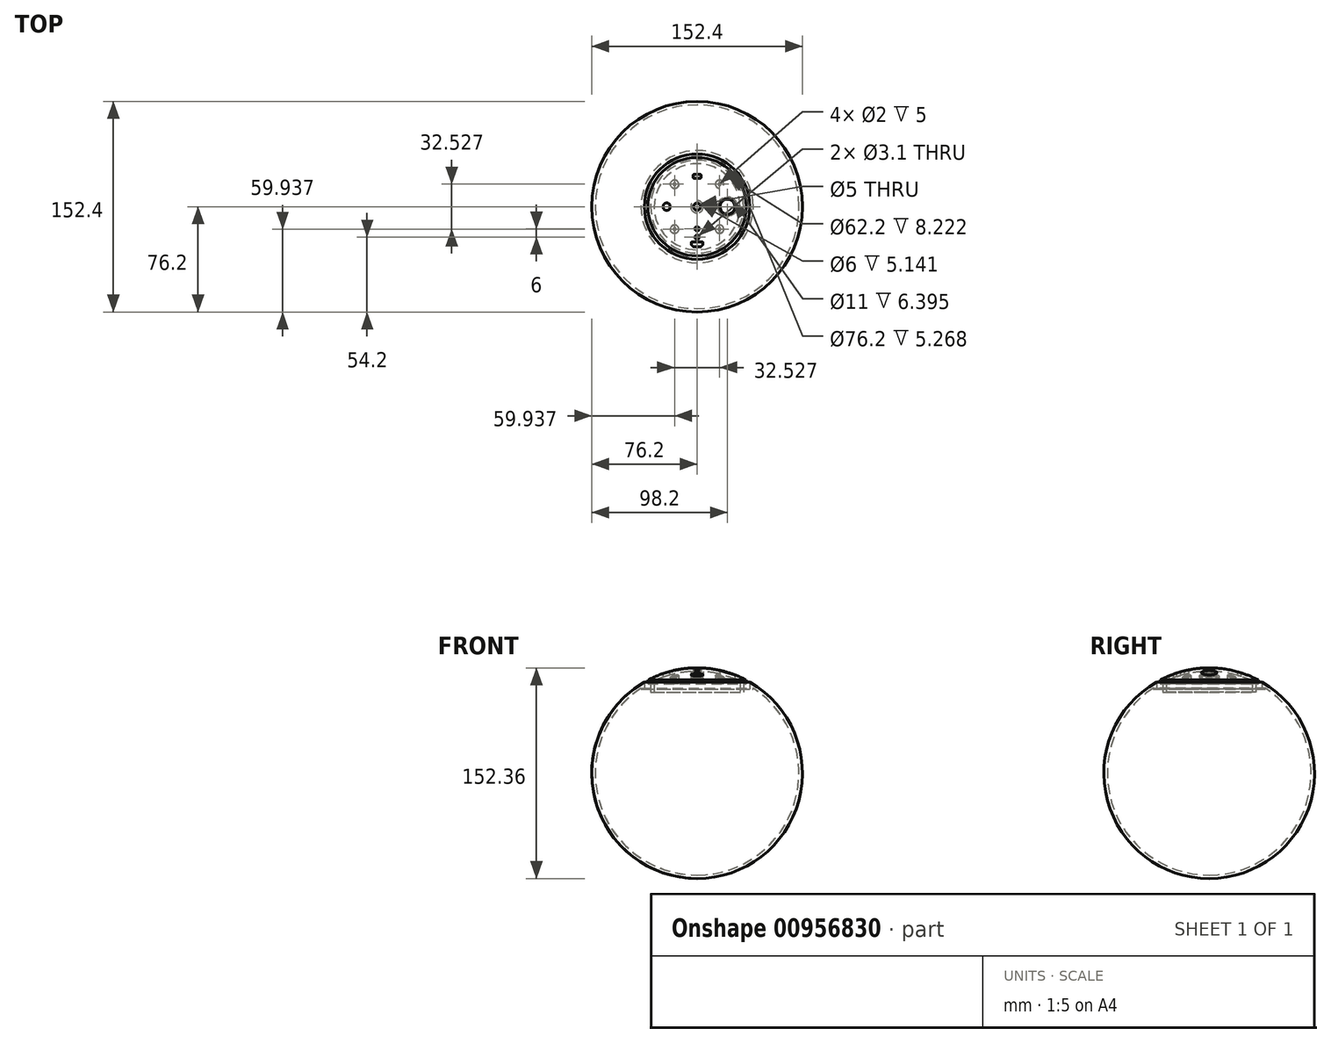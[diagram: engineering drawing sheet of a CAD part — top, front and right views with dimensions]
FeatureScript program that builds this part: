
annotation { "Feature Type Name" : "Feature", "Feature Type Description" : "" }
export const myFeature = defineFeature(function(context is Context, id is Id, definition is map)
    precondition{}
    {
        {
            var Q0;
            Q0=qCreatedBy(makeId("Front.planeOp"),FACE);
            var sketch = newSketch(context, id + "F0", { "sketchPlane" : qUnion([Q0])});
            skArc(sketch, "E0", {"start": v(-38.1, 66) * mm, "mid": v(-73.6, -19.72) * mm, "end": v(0, -76.2) * mm});
            skLineSegment(sketch, "E1", {"start": v(0, 0) * mm, "end": v(0, 126.02) * mm, "construction": true});
            skLineSegment(sketch, "E2.0", {"start": v(38.1, 0) * mm, "end": v(38.1, 126.02) * mm, "construction": true});
            skLineSegment(sketch, "E3.0", {"start": v(-38.1, 0) * mm, "end": v(-38.1, 126.02) * mm, "construction": true});
            skLineSegment(sketch, "E4", {"start": v(0, 0) * mm, "end": v(0, -76.2) * mm, "construction": true});
            skLineSegment(sketch, "E5", {"start": v(0, -76.2) * mm, "end": v(0, -73.7) * mm});
            skLineSegment(sketch, "E6.0", {"start": v(-40.6, 0) * mm, "end": v(-40.6, 61.5) * mm});
            skLineSegment(sketch, "E7", {"start": v(-40.6, 60.72) * mm, "end": v(-38.1, 60.72) * mm});
            skLineSegment(sketch, "E8", {"start": v(-38.1, 60.72) * mm, "end": v(-38.1, 66) * mm});
            skArc(sketch, "E9.trimOffspring", {"start": v(-40.6, 61.5) * mm, "mid": v(-70.59, -21.2) * mm, "end": v(0, -73.7) * mm});
            skSolve(sketch);
        }
        {
            var Q0;
            {var subQ5=sQuery(id+"F0.wireOp",EDGE,"E0");Q0=makeQuery(id+"F0.imprint","IMPRINT",FACE,{"disambiguationData":[TD([[makeQuery(id+"F0.imprint","IMPRINT",EDGE,{"derivedFrom":subQ5}),1.0]])]});}
            var Q1;
            Q1=sQuery(id+"F0.wireOp",EDGE,"E1");
            revolve(context, id + "F1", {"surfaceOperationType" : NewSurfaceOperationType.NEW, "entities" : qUnion([Q0]), "axis" : qUnion([Q1]), "revolveType" : RevolveType.FULL});
        }
        {
            var Q0;
            Q0=qCreatedBy(makeId("Front.planeOp"),FACE);
            var sketch = newSketch(context, id + "F2", { "sketchPlane" : qUnion([Q0])});
            skArc(sketch, "E10", {"start": v(0, 76.2) * mm, "mid": v(-18.34, 73.96) * mm, "end": v(-35.6, 67.37) * mm});
            skLineSegment(sketch, "E11", {"start": v(0, 0) * mm, "end": v(0, 119.66) * mm, "construction": true});
            skLineSegment(sketch, "E12.0", {"start": v(-38.1, 0) * mm, "end": v(-38.1, 119.66) * mm, "construction": true});
            skArc(sketch, "E13.0", {"start": v(0, 73.7) * mm, "mid": v(-15.93, 71.96) * mm, "end": v(-31.1, 66.82) * mm});
            skLineSegment(sketch, "E14.0", {"start": v(-35.6, 64.53) * mm, "end": v(-35.6, 67.37) * mm});
            skLineSegment(sketch, "E15.0", {"start": v(-33.6, 58.6) * mm, "end": v(-33.6, 65.6) * mm});
            skLineSegment(sketch, "E16.0", {"start": v(-31.1, 58.6) * mm, "end": v(-31.1, 66.82) * mm});
            skArc(sketch, "E17.trimOffspring", {"start": v(-33.6, 65.6) * mm, "mid": v(-34.6, 65.07) * mm, "end": v(-35.6, 64.53) * mm});
            skLineSegment(sketch, "E18", {"start": v(-33.6, 58.6) * mm, "end": v(-31.1, 58.6) * mm});
            skLineSegment(sketch, "E19", {"start": v(0, 76.2) * mm, "end": v(0, 73.7) * mm});
            skSolve(sketch);
        }
        {
            var Q0;
            Q0=qSketchRegion(id+"F2",true);
            var Q1;
            Q1=sQuery(id+"F2.wireOp",EDGE,"E11");
            revolve(context, id + "F3", {"surfaceOperationType" : NewSurfaceOperationType.NEW, "entities" : qUnion([Q0]), "axis" : qUnion([Q1]), "revolveType" : RevolveType.FULL});
        }
        {
            var Q0;
            Q0=qCreatedBy(makeId("Top.planeOp"),FACE);
            cPlane(context, id + "F4", {"entities" : qUnion([Q0]), "cplaneType" : CPlaneType.OFFSET, "offset" : 81.28 * mm, "width" : 152.4 * mm, "height" : 152.4 * mm});
        }
        {
            var Q0;
            Q0=qCreatedBy(id+"F4.planeOp",FACE);
            var sketch = newSketch(context, id + "F5", { "sketchPlane" : qUnion([Q0])});
            skLineSegment(sketch, "E20.bottom", {"start": v(3.7, -25.5) * mm, "end": v(-3.7, -25.5) * mm});
            skLineSegment(sketch, "E20.top", {"start": v(4.2, -27.6) * mm, "end": v(-4.2, -27.6) * mm});
            skLineSegment(sketch, "E20.left", {"start": v(4.2, -26) * mm, "end": v(4.2, -27.42) * mm});
            skLineSegment(sketch, "E20.right", {"start": v(-4.2, -26) * mm, "end": v(-4.2, -27.42) * mm});
            skPoint(sketch, "E20.middle", {"position": v(0, -26.55) * mm});
            skLineSegment(sketch, "E21.0", {"start": v(1.38, -28.9) * mm, "end": v(-1.07, -28.9) * mm, "construction": true});
            skLineSegment(sketch, "E22.0", {"start": v(2.7, -21.08) * mm, "end": v(2.7, -25.34) * mm, "construction": true});
            skLineSegment(sketch, "E23.0", {"start": v(-2.7, -21.08) * mm, "end": v(-2.7, -25.34) * mm, "construction": true});
            skLineSegment(sketch, "E24", {"start": v(-4.06, -27.72) * mm, "end": v(-2.81, -28.8) * mm});
            skLineSegment(sketch, "E25", {"start": v(2.81, -28.8) * mm, "end": v(4.06, -27.72) * mm});
            skLineSegment(sketch, "E26", {"start": v(-2.55, -28.9) * mm, "end": v(2.55, -28.9) * mm});
            skPoint(sketch, "E27.visualSharp", {"position": v(-4.2, -25.5) * mm});
            skArc(sketch, "E27.filletArc", {"start": v(-3.7, -25.5) * mm, "mid": v(-4.05, -25.65) * mm, "end": v(-4.2, -26) * mm});
            skPoint(sketch, "E28.visualSharp", {"position": v(4.2, -25.5) * mm});
            skArc(sketch, "E28.filletArc", {"start": v(4.2, -26) * mm, "mid": v(4.05, -25.65) * mm, "end": v(3.7, -25.5) * mm});
            skPoint(sketch, "E29.visualSharp", {"position": v(4.2, -27.6) * mm});
            skArc(sketch, "E29.filletArc", {"start": v(4.06, -27.72) * mm, "mid": v(4.16, -27.58) * mm, "end": v(4.2, -27.42) * mm});
            skPoint(sketch, "E30.visualSharp", {"position": v(2.7, -28.9) * mm});
            skArc(sketch, "E30.filletArc", {"start": v(2.55, -28.9) * mm, "mid": v(2.7, -28.87) * mm, "end": v(2.81, -28.8) * mm});
            skPoint(sketch, "E31.visualSharp", {"position": v(-2.7, -28.9) * mm});
            skArc(sketch, "E31.filletArc", {"start": v(-2.81, -28.8) * mm, "mid": v(-2.7, -28.87) * mm, "end": v(-2.55, -28.9) * mm});
            skPoint(sketch, "E32.visualSharp", {"position": v(-4.2, -27.6) * mm});
            skArc(sketch, "E32.filletArc", {"start": v(-4.2, -27.42) * mm, "mid": v(-4.16, -27.58) * mm, "end": v(-4.06, -27.72) * mm});
            skSolve(sketch);
        }
        {
            var Q0;
            Q0=qCreatedBy(id+"F4.planeOp",FACE);
            var sketch = newSketch(context, id + "F6", { "sketchPlane" : qUnion([Q0])});
            skCircle(sketch, "E33", {"center": v(0, 0) * mm, "radius": 22 * mm, "construction": true});
            skCircle(sketch, "E34", {"center": v(0, -22) * mm, "radius": 1.55 * mm});
            skLineSegment(sketch, "E35", {"start": v(0, 0) * mm, "end": v(0, -21.23) * mm, "construction": true});
            skCircle(sketch, "E36.0.1.0", {"center": v(0, -16) * mm, "radius": 1.55 * mm});
            skLineSegment(sketch, "E36.direction1", {"start": v(0, -22) * mm, "end": v(25, -22) * mm, "construction": true});
            skLineSegment(sketch, "E36.direction2", {"start": v(0, -22) * mm, "end": v(0, -16) * mm, "construction": true});
            skSolve(sketch);
        }
        {
            var Q0;
            Q0=qCreatedBy(id+"F4.planeOp",FACE);
            var sketch = newSketch(context, id + "F7", { "sketchPlane" : qUnion([Q0])});
            skCircle(sketch, "E37", {"center": v(0, 0) * mm, "radius": 22 * mm, "construction": true});
            skCircle(sketch, "E38", {"center": v(22, 0) * mm, "radius": 5.5 * mm});
            skLineSegment(sketch, "E39.bottom", {"start": v(2.8, 23.4) * mm, "end": v(-2.8, 23.4) * mm});
            skLineSegment(sketch, "E39.top", {"start": v(2.8, 20.6) * mm, "end": v(-2.8, 20.6) * mm});
            skLineSegment(sketch, "E39.left", {"start": v(2.8, 23.4) * mm, "end": v(2.8, 20.6) * mm});
            skLineSegment(sketch, "E39.right", {"start": v(-2.8, 23.4) * mm, "end": v(-2.8, 20.6) * mm});
            skPoint(sketch, "E39.middle", {"position": v(0, 22) * mm});
            skSolve(sketch);
        }
        {
            var Q0;
            Q0=qCreatedBy(id+"F4.planeOp",FACE);
            var sketch = newSketch(context, id + "F8", { "sketchPlane" : qUnion([Q0])});
            skCircle(sketch, "E40", {"center": v(0, 0) * mm, "radius": 22 * mm, "construction": true});
            skArc(sketch, "E41", {"start": v(-24.4, -1.24) * mm, "mid": v(-22, -2.7) * mm, "end": v(-19.6, -1.24) * mm});
            skLineSegment(sketch, "E42", {"start": v(-22, 0) * mm, "end": v(-22, 4.73) * mm, "construction": true});
            skLineSegment(sketch, "E43.0", {"start": v(-24.4, -2.74) * mm, "end": v(-24.4, 4.73) * mm});
            skLineSegment(sketch, "E44.MirrorCS", {"start": v(-19.6, -2.74) * mm, "end": v(-19.6, 4.73) * mm});
            skArc(sketch, "E45.trimOffspring", {"start": v(-19.6, 1.24) * mm, "mid": v(-22, 2.7) * mm, "end": v(-24.4, 1.24) * mm});
            skSolve(sketch);
        }
        {
            var Q0;
            Q0=qCreatedBy(id+"F4.planeOp",FACE);
            var sketch = newSketch(context, id + "F9", { "sketchPlane" : qUnion([Q0])});
            skCircle(sketch, "E46", {"center": v(0, 0) * mm, "radius": 2.5 * mm});
            skSolve(sketch);
        }
        {
            var Q0;
            Q0=qSketchRegion(id+"F9",true);
            extrude(context, id + "F10", {"entities" : qUnion([Q0]), "operationType" : NewBodyOperationType.REMOVE, "oppositeDirection" : true, "depth" : 25 * mm, "offsetDistance" : 25 * mm});
        }
        {
            var Q0;
            Q0=qCreatedBy(makeId("Top.planeOp"),FACE);
            cPlane(context, id + "F11", {"entities" : qUnion([Q0]), "cplaneType" : CPlaneType.OFFSET, "offset" : 70 * mm, "width" : 150 * mm, "height" : 150 * mm});
        }
        {
            var Q0;
            Q0=qCreatedBy(id+"F11.planeOp",FACE);
            var sketch = newSketch(context, id + "F12", { "sketchPlane" : qUnion([Q0])});
            skCircle(sketch, "E47", {"center": v(0, 0) * mm, "radius": 3 * mm});
            skSolve(sketch);
        }
        {
            var Q0;
            Q0=qSketchRegion(id+"F12",true);
            var Q1;
            Q1=makeQuery(id+"F3.opRevolve","SWEPT_FACE",FACE,{"disambiguationData":[OSD([sQuery(id+"F2.wireOp",EDGE,"E10")])]});
            extrude(context, id + "F13", {"entities" : qUnion([Q0]), "operationType" : NewBodyOperationType.REMOVE, "endBound" : BoundingType.UP_TO_SURFACE, "depth" : 25 * mm, "endBoundEntityFace" : qUnion([Q1]), "hasOffset" : true, "offsetDistance" : 1 * mm});
        }
        {
            var Q0;
            Q0=qSketchRegion(id+"F5",true);
            extrude(context, id + "F14", {"entities" : qUnion([Q0]), "operationType" : NewBodyOperationType.REMOVE, "oppositeDirection" : true, "depth" : 25.4 * mm, "offsetDistance" : 25.4 * mm});
        }
        {
            var Q0;
            Q0=qSketchRegion(id+"F6",true);
            var Q1;
            Q1=qSketchRegion(id+"F8",true);
            extrude(context, id + "F15", {"entities" : qUnion([Q0, Q1]), "operationType" : NewBodyOperationType.REMOVE, "oppositeDirection" : true, "depth" : 25 * mm, "offsetDistance" : 25 * mm});
        }
        {
            var Q0;
            Q0=qSketchRegion(id+"F7",true);
            extrude(context, id + "F16", {"entities" : qUnion([Q0]), "operationType" : NewBodyOperationType.REMOVE, "oppositeDirection" : true, "depth" : 25 * mm, "offsetDistance" : 25 * mm});
        }
        {
            var Q0;
            Q0=qCreatedBy(makeId("Top.planeOp"),FACE);
            cPlane(context, id + "F17", {"entities" : qUnion([Q0]), "cplaneType" : CPlaneType.OFFSET, "offset" : 65 * mm, "width" : 150 * mm, "height" : 150 * mm});
        }
        {
            var Q0;
            Q0=qCreatedBy(id+"F17.planeOp",FACE);
            var sketch = newSketch(context, id + "F18", { "sketchPlane" : qUnion([Q0])});
            skCircle(sketch, "E48", {"center": v(-16.26, 16.26) * mm, "radius": 3 * mm});
            skLineSegment(sketch, "E49", {"start": v(0, 0) * mm, "end": v(-28.69, 28.69) * mm, "construction": true});
            skLineSegment(sketch, "E50", {"start": v(0, 0) * mm, "end": v(16.68, 16.68) * mm, "construction": true});
            skCircle(sketch, "E51.1.0", {"center": v(-16.26, -16.26) * mm, "radius": 3 * mm});
            skCircle(sketch, "E51.2.0", {"center": v(16.26, -16.26) * mm, "radius": 3 * mm});
            skCircle(sketch, "E51.3.0", {"center": v(16.26, 16.26) * mm, "radius": 3 * mm});
            skPoint(sketch, "E51.center", {"position": v(0, 0) * mm});
            skSolve(sketch);
        }
        {
            var Q0;
            Q0=qSketchRegion(id+"F18",true);
            var Q1;
            Q1=makeQuery(id+"F3.opRevolve","SWEPT_FACE",FACE,{"disambiguationData":[OSD([sQuery(id+"F2.wireOp",EDGE,"E13.0")])]});
            extrude(context, id + "F19", {"entities" : qUnion([Q0]), "operationType" : NewBodyOperationType.ADD, "endBound" : BoundingType.UP_TO_SURFACE, "depth" : 25 * mm, "endBoundEntityFace" : qUnion([Q1]), "offsetDistance" : 25 * mm});
        }
        {
            var Q0;
            Q0=qCreatedBy(id+"F17.planeOp",FACE);
            var sketch = newSketch(context, id + "F20", { "sketchPlane" : qUnion([Q0])});
            skCircle(sketch, "E52.0", {"center": v(-16.26, 16.26) * mm, "radius": 3 * mm, "construction": true});
            skCircle(sketch, "E53", {"center": v(-16.26, 16.26) * mm, "radius": 1 * mm});
            skCircle(sketch, "E54.1.0", {"center": v(-16.26, -16.26) * mm, "radius": 1 * mm});
            skCircle(sketch, "E54.2.0", {"center": v(16.26, -16.26) * mm, "radius": 1 * mm});
            skCircle(sketch, "E54.3.0", {"center": v(16.26, 16.26) * mm, "radius": 1 * mm});
            skPoint(sketch, "E54.center", {"position": v(0, 0) * mm});
            skSolve(sketch);
        }
        {
            var Q0;
            Q0=qSketchRegion(id+"F20",true);
            extrude(context, id + "F21", {"entities" : qUnion([Q0]), "operationType" : NewBodyOperationType.REMOVE, "depth" : 5 * mm, "offsetDistance" : 25 * mm});
        }
        {
            var Q0;
            Q0=qCreatedBy(makeId("Top.planeOp"),FACE);
            cPlane(context, id + "F22", {"entities" : qUnion([Q0]), "cplaneType" : CPlaneType.OFFSET, "offset" : 68 * mm, "width" : 150 * mm, "height" : 150 * mm});
        }
        {
            var Q0;
            Q0=qCreatedBy(id+"F22.planeOp",FACE);
            var sketch = newSketch(context, id + "F23", { "sketchPlane" : qUnion([Q0])});
            skCircle(sketch, "E55.0", {"center": v(22, 0) * mm, "radius": 5.5 * mm});
            skCircle(sketch, "E56.0", {"center": v(22, 0) * mm, "radius": 7 * mm});
            skSolve(sketch);
        }
        {
            var Q0;
            Q0=qSketchRegion(id+"F23",true);
            var Q1;
            Q1=makeQuery(id+"F3.opRevolve","SWEPT_FACE",FACE,{"disambiguationData":[OSD([sQuery(id+"F2.wireOp",EDGE,"E13.0")])]});
            extrude(context, id + "F24", {"entities" : qUnion([Q0]), "operationType" : NewBodyOperationType.ADD, "endBound" : BoundingType.UP_TO_SURFACE, "depth" : 25 * mm, "endBoundEntityFace" : qUnion([Q1]), "offsetDistance" : 25 * mm});
        }
        {
            var Q0;
            Q0=qCreatedBy(id+"F22.planeOp",FACE);
            var sketch = newSketch(context, id + "F25", { "sketchPlane" : qUnion([Q0])});
            skCircle(sketch, "E57.0", {"center": v(22, 0) * mm, "radius": 5.5 * mm, "construction": true});
            skCircle(sketch, "E58.0", {"center": v(22, 0) * mm, "radius": 5.45 * mm});
            skSolve(sketch);
        }
        {
            var Q0;
            Q0=qSketchRegion(id+"F25",true);
            var Q1;
            Q1=makeQuery(id+"F3.opRevolve","SWEPT_FACE",FACE,{"disambiguationData":[OSD([sQuery(id+"F2.wireOp",EDGE,"E10")])]});
            extrude(context, id + "F26", {"entities" : qUnion([Q0]), "endBound" : BoundingType.UP_TO_SURFACE, "depth" : 25 * mm, "endBoundEntityFace" : qUnion([Q1]), "offsetDistance" : 25 * mm});
        }
        {
            var Q0;
            Q0=makeQuery(id+"F26.opExtrude","CAP_FACE",FACE,{"disambiguationData":[OSD([sQuery(id+"F25.wireOp",EDGE,"E58.0")])],"isStart":true});
            var sketch = newSketch(context, id + "F27", { "sketchPlane" : qUnion([Q0])});
            skCircle(sketch, "E59", {"center": v(22, 0) * mm, "radius": 6.5 * mm});
            skSolve(sketch);
        }
        {
            var Q0;
            Q0=qSketchRegion(id+"F27",true);
            extrude(context, id + "F28", {"entities" : qUnion([Q0]), "operationType" : NewBodyOperationType.ADD, "depth" : 1 * mm, "offsetDistance" : 25 * mm});
        }
        {
            var Q0;
            Q0=qCreatedBy(id+"F11.planeOp",FACE);
            var sketch = newSketch(context, id + "F29", { "sketchPlane" : qUnion([Q0])});
            skCircle(sketch, "E60.0", {"center": v(0, 0) * mm, "radius": 3 * mm});
            skCircle(sketch, "E61.0", {"center": v(0, 0) * mm, "radius": 4.5 * mm});
            skSolve(sketch);
        }
        {
            var Q0;
            Q0=qSketchRegion(id+"F29",true);
            var Q1;
            Q1=makeQuery(id+"F3.opRevolve","SWEPT_FACE",FACE,{"disambiguationData":[OSD([sQuery(id+"F2.wireOp",EDGE,"E13.0")])]});
            extrude(context, id + "F30", {"entities" : qUnion([Q0]), "operationType" : NewBodyOperationType.ADD, "endBound" : BoundingType.UP_TO_SURFACE, "depth" : 25 * mm, "endBoundEntityFace" : qUnion([Q1]), "offsetDistance" : 25 * mm});
        }
        {
            var Q0;
            Q0=makeQuery(id+"F16.boolean.opBoolean","COPY",EDGE,{"derivedFrom":makeQuery(id+"F16.opExtrude","SWEPT_EDGE",EDGE,{"disambiguationData":[OSD([sQuery(id+"F7.wireOp",EDGE,"E39.bottom"),sQuery(id+"F7.wireOp",EDGE,"E39.right")])]})});
            var Q1;
            Q1=makeQuery(id+"F16.boolean.opBoolean","COPY",EDGE,{"derivedFrom":makeQuery(id+"F16.opExtrude","SWEPT_EDGE",EDGE,{"disambiguationData":[OSD([sQuery(id+"F7.wireOp",EDGE,"E39.top"),sQuery(id+"F7.wireOp",EDGE,"E39.right")])]})});
            var Q2;
            Q2=makeQuery(id+"F16.boolean.opBoolean","COPY",EDGE,{"derivedFrom":makeQuery(id+"F16.opExtrude","SWEPT_EDGE",EDGE,{"disambiguationData":[OSD([sQuery(id+"F7.wireOp",EDGE,"E39.top"),sQuery(id+"F7.wireOp",EDGE,"E39.left")])]})});
            var Q3;
            Q3=makeQuery(id+"F16.boolean.opBoolean","COPY",EDGE,{"derivedFrom":makeQuery(id+"F16.opExtrude","SWEPT_EDGE",EDGE,{"disambiguationData":[OSD([sQuery(id+"F7.wireOp",EDGE,"E39.bottom"),sQuery(id+"F7.wireOp",EDGE,"E39.left")])]})});
            fillet(context, id + "F31", {"entities" : qUnion([Q0, Q1, Q2, Q3]), "radius" : .5 * mm, "tangentPropagation" : true, "allowEdgeOverflow" : false});
        }
    });
